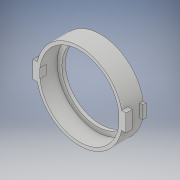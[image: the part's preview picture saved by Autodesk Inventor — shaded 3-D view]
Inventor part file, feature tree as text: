
AUTODESK INVENTOR PART (.ipt)
format: ipt  version: 2018 (Build 220112000, 112)  size: 158,208 bytes
history: native  units: in
note: dims shown in document units (in); Inventor stores cm internally (conversion verified against a paired STEP export)
features: extrude x5, sketch x5
ambient origin geometry x8: Origin, YZ Plane, XZ Plane, XY Plane, X Axis, Y Axis, Z Axis, Center Point
bodies: Solid1 (feature_tree)
feature tree (10):
  extrude  "Extrusion1"  Depth=0.3in TaperAngle=0.0deg
  extrude  "Extrusion2"  Depth=0.25in TaperAngle=0.0deg
  extrude  "Extrusion3"  Depth=0.247in
  extrude  "Extrusion5"  Depth=0.247in
  extrude  "Extrusion6"  Depth=0.05in
  sketch  "Sketch1"  dims[d0=1.225in d1=0.3in d2=0.0in]
  sketch  "Sketch2"  dims[d3=0.25in d4=0.0in d5=0.2in d6=0.0in]
  sketch  "Sketch3"  dims[d7=0.1in d8=0.247in]
  sketch  "Sketch4"  dims[d9=0.1in d10=0.247in]
  sketch  "Sketch5"  dims[d13=0.09in d14=0.0in d15=1.0in d16=1.133in d17=0.1in d18=0.1in d19=0.6in d20=0.6in d21=0.05in d22=0.0in]
